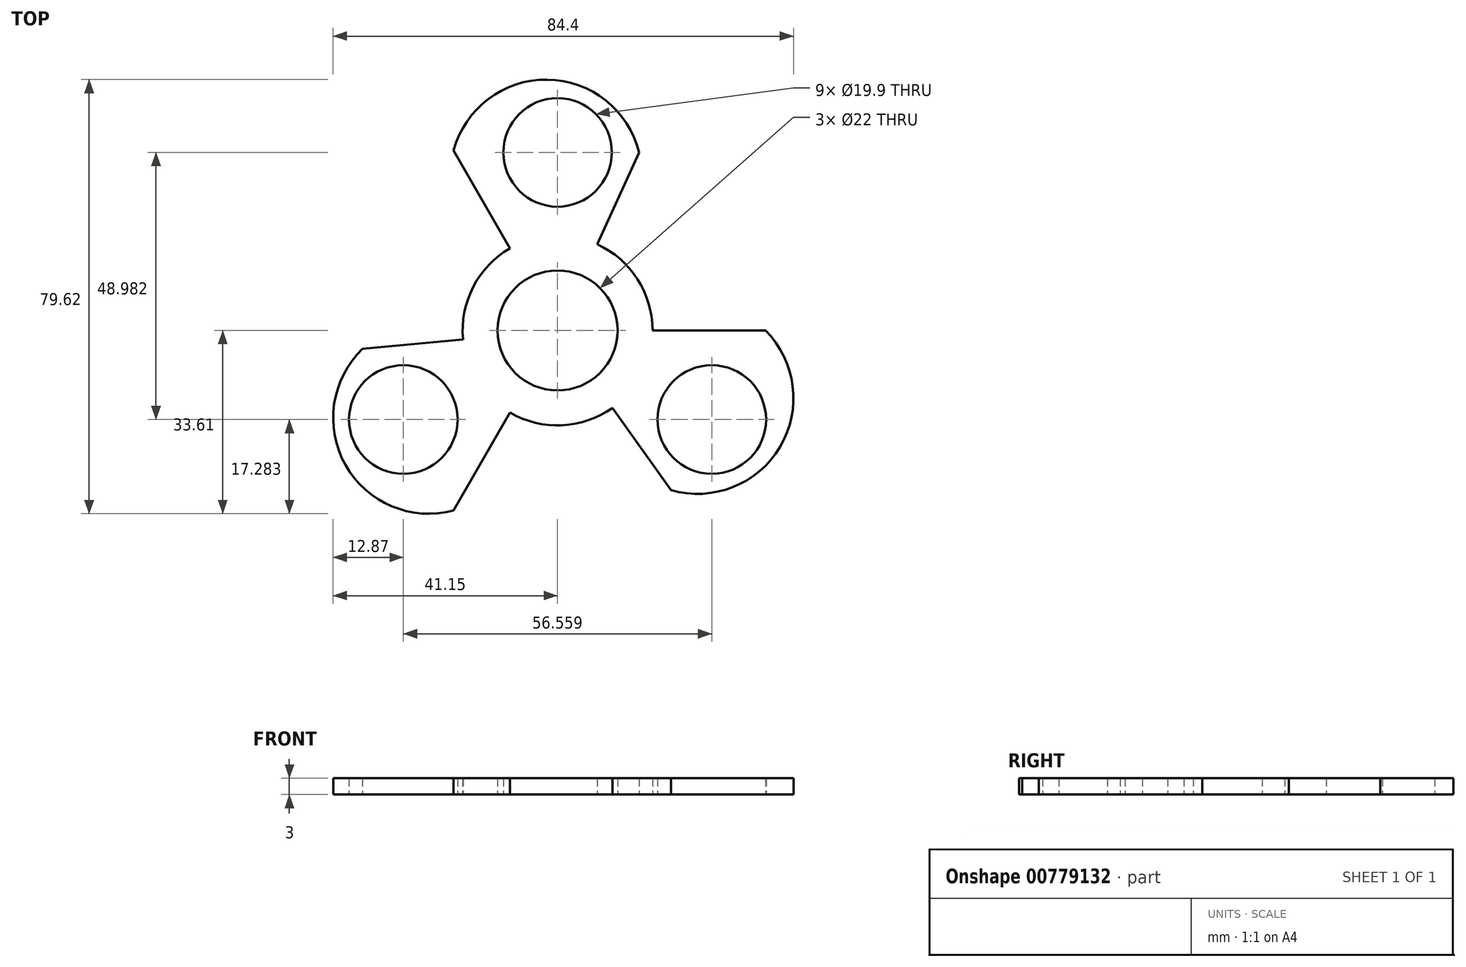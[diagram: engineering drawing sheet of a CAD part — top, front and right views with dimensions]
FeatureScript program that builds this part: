
annotation { "Feature Type Name" : "Feature", "Feature Type Description" : "" }
export const myFeature = defineFeature(function(context is Context, id is Id, definition is map)
    precondition{}
    {
        {
            var Q0;
            Q0=qCreatedBy(makeId("Top.planeOp"),FACE);
            var sketch = newSketch(context, id + "F0", { "sketchPlane" : qUnion([Q0])});
            skArc(sketch, "E0", {"start": v(9.53, 5.5) * mm, "mid": v(0, 11) * mm, "end": v(-9.53, 5.5) * mm});
            skCircle(sketch, "E1", {"center": v(0, 32.65) * mm, "radius": 9.95 * mm});
            skArc(sketch, "E2", {"start": v(14.94, 32.65) * mm, "mid": v(-1.92, 46) * mm, "end": v(-19.06, 33.01) * mm});
            skLineSegment(sketch, "E3", {"start": v(-19.06, 33.01) * mm, "end": v(-8.7, 15.08) * mm});
            skLineSegment(sketch, "E4", {"start": v(14.94, 32.65) * mm, "end": v(7.24, 15.83) * mm});
            skArc(sketch, "E5", {"start": v(15.08, 8.7) * mm, "mid": v(11.72, 12.88) * mm, "end": v(7.24, 15.83) * mm});
            skArc(sketch, "E6.trimOffspring", {"start": v(-8.7, 15.08) * mm, "mid": v(-12.31, 12.31) * mm, "end": v(-15.08, 8.7) * mm});
            skLineSegment(sketch, "E7.1.1", {"start": v(-35.75, -3.39) * mm, "end": v(-17.33, -1.64) * mm});
            skCircle(sketch, "E7.1.2", {"center": v(-28.28, -16.33) * mm, "radius": 9.95 * mm});
            skArc(sketch, "E7.1.3", {"start": v(-9.53, 5.5) * mm, "mid": v(-9.53, -5.5) * mm, "end": v(0, -11) * mm});
            skArc(sketch, "E7.1.4", {"start": v(-35.75, -3.39) * mm, "mid": v(-38.88, -24.67) * mm, "end": v(-19.06, -33.01) * mm});
            skArc(sketch, "E7.1.5", {"start": v(-15.08, 8.7) * mm, "mid": v(-17.01, 3.7) * mm, "end": v(-17.33, -1.64) * mm});
            skArc(sketch, "E7.1.6", {"start": v(-8.7, -15.08) * mm, "mid": v(-4.5, -16.82) * mm, "end": v(0, -17.41) * mm});
            skLineSegment(sketch, "E7.1.7", {"start": v(-19.06, -33.01) * mm, "end": v(-8.7, -15.08) * mm});
            skLineSegment(sketch, "E7.2.1", {"start": v(20.8, -29.27) * mm, "end": v(10.09, -14.19) * mm});
            skCircle(sketch, "E7.2.2", {"center": v(28.28, -16.33) * mm, "radius": 9.95 * mm});
            skArc(sketch, "E7.2.3", {"start": v(0, -11) * mm, "mid": v(9.53, -5.5) * mm, "end": v(9.53, 5.5) * mm});
            skArc(sketch, "E7.2.4", {"start": v(20.8, -29.27) * mm, "mid": v(40.8, -21.34) * mm, "end": v(38.12, 0) * mm});
            skArc(sketch, "E7.2.5", {"start": v(0, -17.41) * mm, "mid": v(5.3, -16.59) * mm, "end": v(10.09, -14.19) * mm});
            skArc(sketch, "E7.2.6", {"start": v(17.41, 0) * mm, "mid": v(16.82, 4.5) * mm, "end": v(15.08, 8.7) * mm});
            skLineSegment(sketch, "E7.2.7", {"start": v(38.12, 0) * mm, "end": v(17.41, 0) * mm});
            skLineSegment(sketch, "E8.trimOffspring", {"start": v(0, 45.88) * mm, "end": v(0, 50) * mm});
            skSolve(sketch);
        }
        {
            var Q0;
            Q0 = qSketchRegion(id + "F0", true);
            extrude(context, id + "F1", {"entities" : qUnion([Q0]), "depth" : 3 * mm, "offsetDistance" : 25 * mm});
        }
    });
